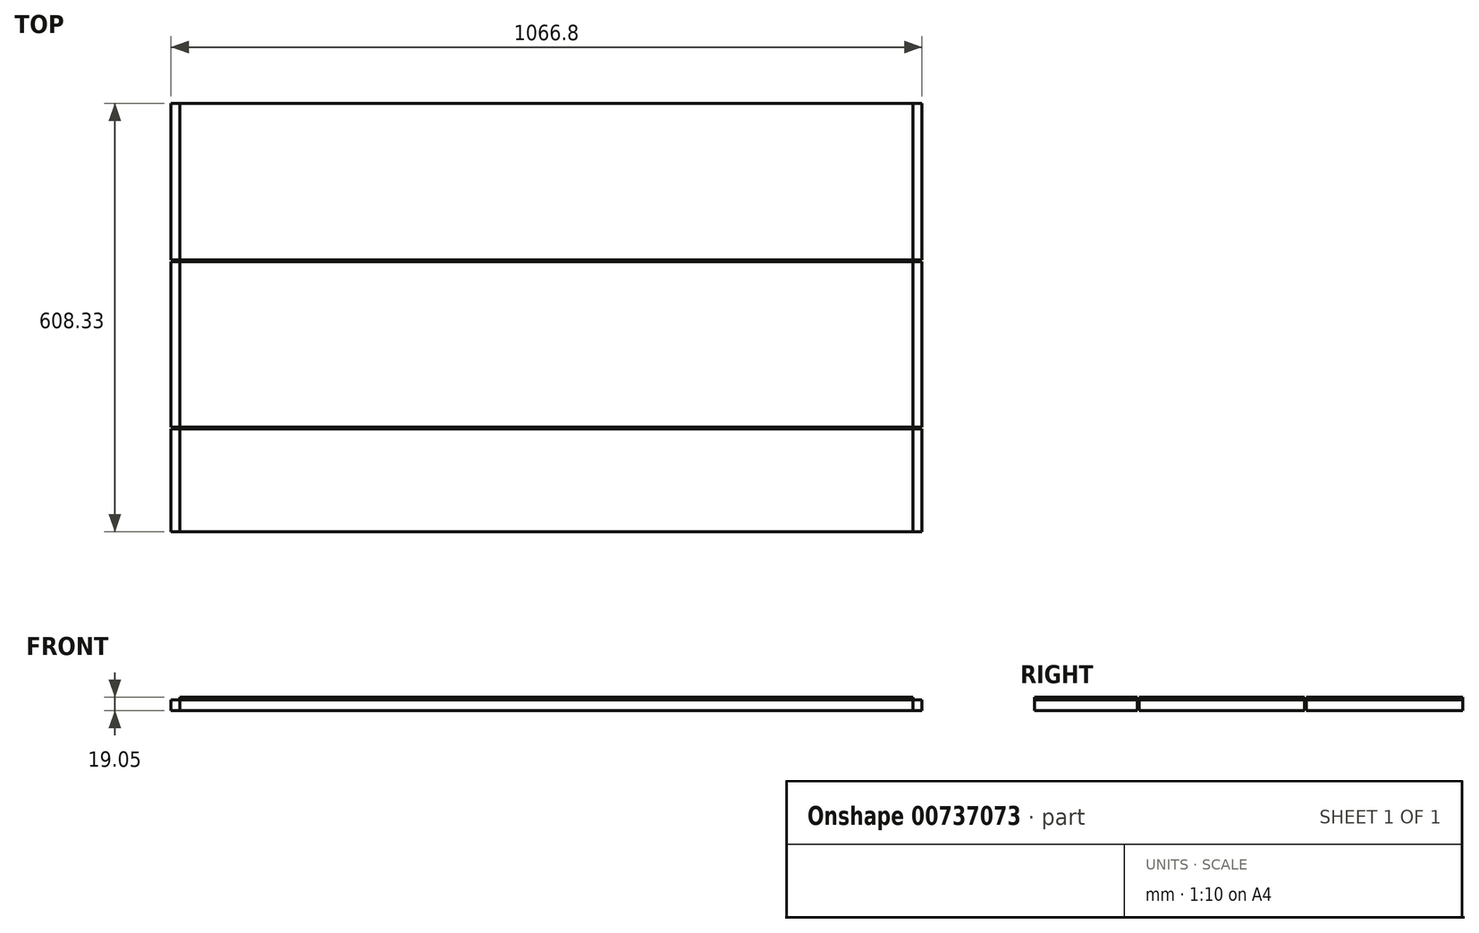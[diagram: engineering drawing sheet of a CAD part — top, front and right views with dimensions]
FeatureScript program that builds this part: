
annotation { "Feature Type Name" : "Feature", "Feature Type Description" : "" }
export const myFeature = defineFeature(function(context is Context, id is Id, definition is map)
    precondition{}
    {
        {
            var Q0;
            Q0=qCreatedBy(makeId("Top.planeOp"),FACE);
            var sketch = newSketch(context, id + "F0", { "sketchPlane" : qUnion([Q0])});
            skLineSegment(sketch, "E0.bottom", {"start": v(-549.37, -291.63) * mm, "end": v(517.43, -291.63) * mm});
            skLineSegment(sketch, "E0.top", {"start": v(-549.37, -56.68) * mm, "end": v(517.43, -56.68) * mm});
            skLineSegment(sketch, "E0.left", {"start": v(-549.37, -291.63) * mm, "end": v(-549.37, -56.68) * mm});
            skLineSegment(sketch, "E0.right", {"start": v(517.43, -291.63) * mm, "end": v(517.43, -56.68) * mm});
            skLineSegment(sketch, "E1.bottom", {"start": v(-549.37, -54.14) * mm, "end": v(517.43, -54.14) * mm});
            skLineSegment(sketch, "E1.top", {"start": v(-549.37, 168.1) * mm, "end": v(517.43, 168.1) * mm});
            skLineSegment(sketch, "E1.left", {"start": v(-549.37, -54.14) * mm, "end": v(-549.37, 168.1) * mm});
            skLineSegment(sketch, "E1.right", {"start": v(517.43, -54.14) * mm, "end": v(517.43, 168.1) * mm});
            skLineSegment(sketch, "E2.bottom", {"start": v(-549.37, -440.22) * mm, "end": v(517.43, -440.22) * mm});
            skLineSegment(sketch, "E2.top", {"start": v(-549.37, -294.17) * mm, "end": v(517.43, -294.17) * mm});
            skLineSegment(sketch, "E2.left", {"start": v(-549.37, -440.22) * mm, "end": v(-549.37, -294.17) * mm});
            skLineSegment(sketch, "E2.right", {"start": v(517.43, -440.22) * mm, "end": v(517.43, -294.17) * mm});
            skLineSegment(sketch, "E3", {"start": v(-536.67, 168.1) * mm, "end": v(-536.67, -54.14) * mm});
            skLineSegment(sketch, "E4", {"start": v(-536.67, -56.68) * mm, "end": v(-536.67, -291.63) * mm});
            skLineSegment(sketch, "E5", {"start": v(-536.67, -294.17) * mm, "end": v(-536.67, -440.22) * mm});
            skLineSegment(sketch, "E6", {"start": v(504.73, -440.22) * mm, "end": v(504.73, -294.17) * mm});
            skLineSegment(sketch, "E7", {"start": v(504.73, -56.68) * mm, "end": v(504.73, -291.63) * mm});
            skLineSegment(sketch, "E8", {"start": v(504.73, -54.14) * mm, "end": v(504.73, 168.1) * mm});
            skSolve(sketch);
        }
        {
            var Q0;
            Q0 = qSketchRegion(id + "F0", true);
            extrude(context, id + "F1", {"entities" : qUnion([Q0]), "depth" : 15.24 * mm, "offsetDistance" : 25.4 * mm});
        }
        {
            var Q0;
            {var subQ0=sQuery(id+"F0.wireOp",EDGE,"E5");Q0=makeQuery(id+"F0.imprint","IMPRINT",FACE,{"disambiguationData":[TD([[makeQuery(id+"F0.imprint","IMPRINT",EDGE,{"derivedFrom":subQ0}),1.0]])]});}
            var Q1;
            {var subQ0=sQuery(id+"F0.wireOp",EDGE,"E4");Q1=makeQuery(id+"F0.imprint","IMPRINT",FACE,{"disambiguationData":[TD([[makeQuery(id+"F0.imprint","IMPRINT",EDGE,{"derivedFrom":subQ0}),1.0]])]});}
            var Q2;
            {var subQ0=sQuery(id+"F0.wireOp",EDGE,"E3");Q2=makeQuery(id+"F0.imprint","IMPRINT",FACE,{"disambiguationData":[TD([[makeQuery(id+"F0.imprint","IMPRINT",EDGE,{"derivedFrom":subQ0}),1.0]])]});}
            extrude(context, id + "F2", {"entities" : qUnion([Q0, Q1, Q2]), "depth" : 19.05 * mm, "offsetDistance" : 25.4 * mm});
        }
    });
